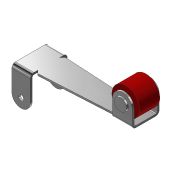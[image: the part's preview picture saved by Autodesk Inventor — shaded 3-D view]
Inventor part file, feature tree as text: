
AUTODESK INVENTOR PART (.ipt)
format: ipt  version: 2014 SP2 (Build 180247200, 247)  size: 245,248 bytes
history: native  units: mm
features: sheet_metal_op x9, sketch x8, other x4, chamfer x2, hole x2, plane x1, revolve x1, extrude x1, mirror x1
ambient origin geometry x8: Origin, YZ Plane, XZ Plane, XY Plane, X Axis, Y Axis, Z Axis, Center Point
bodies: Solid1 (feature_tree)
feature tree (29):
  sheet_metal_op  "Face1"
  sheet_metal_op  "Flange1"
  chamfer  "Corner Round1"
  sheet_metal_op  "Face2"
  sheet_metal_op  "Flange2"
  chamfer  "Corner Round2"
  hole  "Hole1"  [1 undecoded]
  hole  "Hole2"  [1 undecoded]
  plane  "Work Plane1"
  revolve  "Revolution1"  [1 undecoded]
  extrude  "Extrusion1"  Depth=0.6mm
  mirror  "Mirror1"
  sketch  "Sketch2"  dims[d2=6.0mm d3=3.0mm]
  other  "Plate1"
  sketch  "Sketch3"  dims[d4=3.0mm d5=1.5mm]
  other  "Plate2"
  sheet_metal_op  "Bend1"
  sheet_metal_op  "Corner1"
  sketch  "Sketch4"  dims[d6=0.3mm d7=0.3mm]
  other  "Plate3"
  sheet_metal_op  "Bend2"
  sketch  "Sketch5"  dims[d8=0.15mm d9=0.6mm]
  other  "Plate4"
  sheet_metal_op  "Bend3"
  sheet_metal_op  "Corner2"
  sketch  "Sketch6"  dims[d10=0.3mm]
  sketch  "Sketch7"  dims[d11=5.5mm d12=90.0deg d13=0.3mm]
  sketch  "Sketch8"  dims[d14=1.2mm]
  sketch  "Sketch9"  dims[d15=0.3mm d16=0.3mm d17=1.5mm d18=15.75mm d19=3.5mm d20=3.5mm d21=3.2mm d22=1.6mm d23=4.5mm d24=2.25mm d25=0.5mm d26=0.5mm d27=3.5mm d28=1.75mm d29=0.3mm d30=0.3mm d31=0.15mm d32=0.6mm d33=0.3mm d34=0.3mm d35=0.15mm d36=0.6mm d37=0.3mm d38=4.5mm d39=90.0deg d40=0.3mm d41=1.2mm d42=0.3mm d43=0.3mm d44=1.6mm d45=0.8mm d46=6.0mm d47=4.0mm d48=2.0mm d49=90.0deg d50=0.3mm d51=20.594885mm d52=1.5mm d53=6.0mm d54=4.0mm d55=2.0mm d56=90.0deg d57=0.3mm d58=20.594885mm d59=0.25mm d60=0.25mm d61=2.25mm d62=0.75mm d63=4.4mm d64=4.4mm d65=90.0deg d66=2.0mm d67=0.3mm d68=0.0mm d71=17.0mm]
note: 3 required parameter values undecoded (feature->parameter linkage not recoverable at this tier; creation-order binding heuristic only, values carry confidence <= 0.55)